# Revit family: ADB Gas cooktops cupboard 800
name_source: partatom
category: Equipement spécialisé
units: mm (PartAtom-declared; Revit-internal decimal feet)

## family parameters
Basée sur le plan de construction = Non
Conserver l'orientation des annotations = Non
Cote de connecteur circulaire = Utiliser le diamètre
Couper avec des vides une fois chargée = Non
Numéro OmniClass = 23.40.40.14.17.11
Partagée = Non
Repère de localisation dans la pièce = Non
Titre OmniClass = Cookers, Ovens, Stoves
Toujours verticalement = Oui
Type d'élément = Normal

## types (5) — shared parameters
C = 400 mm  [stored 1.31234 ft]
Commentaires du type = Ambassade range - Cupboards - Gas cooktops
D = 765 mm  [stored 2.50984 ft]
E = 50 mm  [stored 0.164042 ft]
Electric power = 0 W
Electrical Remarks = 230V(MONO) commutable 400V(TRI)
F = 810 mm
Fabricant = Société Industrielle de Lacanche
Gas Flow = 0.0 L/s
Gas Size = 20.96 mm
Operational Current = 0 A
URL = https://www.ambassade-de-bourgogne.com
URL Cutsheet = https://www.ambassade-de-bourgogne.com
zero-valued in all types: Elévation par défaut

## per-type parameters (varying)
| type | Bouton 840 | Description | Gas power kW | Plaque | Poids base | Tout sauf 820 |
| CMG 830 | Non | 5kW+2x3kW burner cupboard | 13 | CMG 800 - 4-3-2 feux vifs et plaque : CMG 830 / 830 XR | 73.00 kg | Oui |
| CMG 830 XR | Non | 7kW+2x3kW burner cupboard | 13 | CMG 800 - 4-3-2 feux vifs et plaque : CMG 830 / 830 XR | 83.00 kg | Oui |
| CMG 830 CF | Non | 5kW+2x3kW burner - Cast iron simmer plate cupboard | 13 | CMG 800 - 4-3-2 feux vifs et plaque : CMG 830 CF | 83.00 kg | Oui |
| CMG 820 GCF | Non | 7kW burner - Cast iron simmer plate cupboard | 9 | CMG 800 - 4-3-2 feux vifs et plaque : CMG 820 CGF | 87.00 kg | Non |
| CMG 840 | Oui | 2x4kW+2x3kW burner cupboard | 16 | CMG 800 - 4-3-2 feux vifs et plaque : CMG 840 | 75.00 kg | Oui |

note: column(s) folded — value = type name in every type: Modèle

note: [stored X ft] marks values corroborated as IEEE doubles in the binary element streams (Revit-internal decimal feet)
